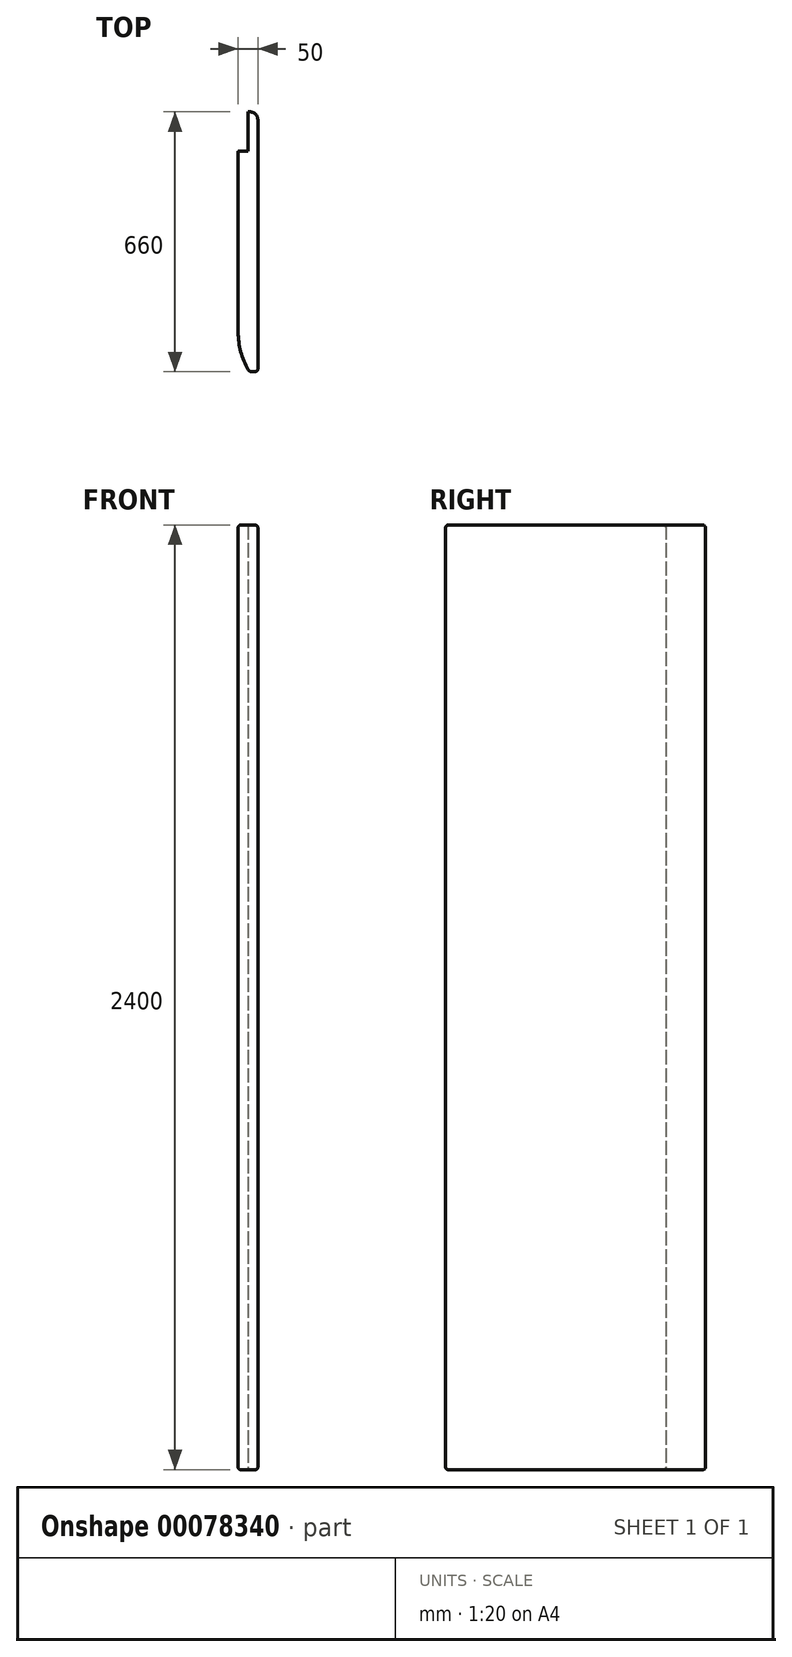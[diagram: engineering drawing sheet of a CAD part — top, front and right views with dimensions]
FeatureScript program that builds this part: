
annotation { "Feature Type Name" : "Feature", "Feature Type Description" : "" }
export const myFeature = defineFeature(function(context is Context, id is Id, definition is map)
    precondition{}
    {
        {
            var Q0;
            Q0=qCreatedBy(makeId("Top.planeOp"),FACE);
            var sketch = newSketch(context, id + "F0", { "sketchPlane" : qUnion([Q0])});
            skLineSegment(sketch, "E0.bottom", {"start": v(-25, 301.84) * mm, "end": v(-20, 301.84) * mm});
            skLineSegment(sketch, "E0.top", {"start": v(-16.2, -358.16) * mm, "end": v(-6.5, -358.16) * mm});
            skLineSegment(sketch, "E0.left", {"start": v(-50, 201.84) * mm, "end": v(-50, -258.16) * mm});
            skLineSegment(sketch, "E0.right", {"start": v(0, 281.84) * mm, "end": v(0, -351.66) * mm});
            skArc(sketch, "E1", {"start": v(-50, -258.16) * mm, "mid": v(-43.5, -307.48) * mm, "end": v(-24.41, -353.42) * mm});
            skLineSegment(sketch, "E2.bottom", {"start": v(-50, 201.84) * mm, "end": v(-25, 201.84) * mm});
            skLineSegment(sketch, "E2.right", {"start": v(-25, 201.84) * mm, "end": v(-25, 301.84) * mm});
            skPoint(sketch, "E3.visualSharp", {"position": v(0, -358.16) * mm});
            skArc(sketch, "E3.filletArc", {"start": v(-6.5, -358.16) * mm, "mid": v(-1.9, -356.26) * mm, "end": v(0, -351.66) * mm});
            skPoint(sketch, "E4.visualSharp", {"position": v(-21.57, -358.16) * mm});
            skArc(sketch, "E4.filletArc", {"start": v(-24.41, -353.42) * mm, "mid": v(-20.94, -356.9) * mm, "end": v(-16.2, -358.16) * mm});
            skPoint(sketch, "E5.visualSharp", {"position": v(0, 301.84) * mm});
            skArc(sketch, "E5.filletArc", {"start": v(0, 281.84) * mm, "mid": v(-5.86, 295.98) * mm, "end": v(-20, 301.84) * mm});
            skSolve(sketch);
        }
        {
            var Q0;
            Q0=makeQuery(id+"F0.imprint","IMPRINT",FACE,{"disambiguationData":[TD([[makeQuery(id+"F0.imprint","IMPRINT",EDGE,{"derivedFrom":sQuery(id+"F0.wireOp",EDGE,"E0.bottom")}),-1.0]])]});
            extrude(context, id + "F1", {"entities" : qUnion([Q0]), "depth" : 2400 * mm});
        }
        {
            var Q0;
            Q0=makeQuery(id+"F1.opExtrude","CAP_EDGE",EDGE,{"disambiguationData":[OSD([sQuery(id+"F0.wireOp",EDGE,"E0.left")])],"isStart":false});
            var Q1;
            Q1=makeQuery(id+"F1.opExtrude","CAP_EDGE",EDGE,{"disambiguationData":[OSD([sQuery(id+"F0.wireOp",EDGE,"E0.left")])],"isStart":true});
            fillet(context, id + "F2", {"entities" : qUnion([Q0, Q1]), "radius" : 6.5 * mm, "tangentPropagation" : true, "allowEdgeOverflow" : false});
        }
    });
